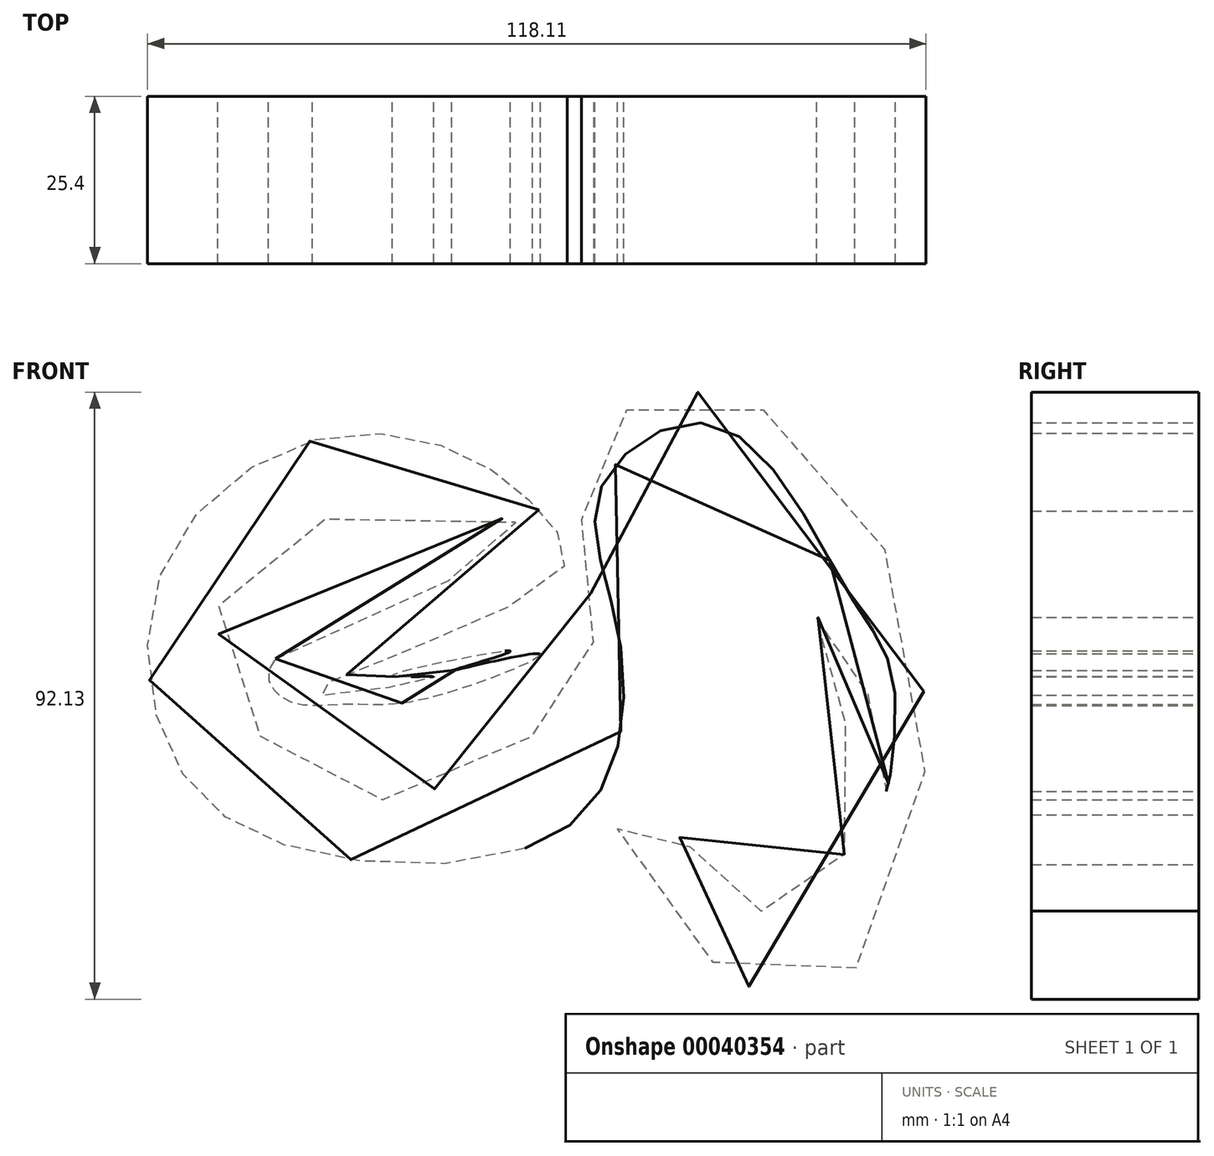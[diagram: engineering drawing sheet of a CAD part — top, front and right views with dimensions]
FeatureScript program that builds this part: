
annotation { "Feature Type Name" : "Feature", "Feature Type Description" : "" }
export const myFeature = defineFeature(function(context is Context, id is Id, definition is map)
    precondition{}
    {
        {
            var Q0;
            Q0=qCreatedBy(makeId("Front.planeOp"),FACE);
            var sketch = newSketch(context, id + "F0", { "sketchPlane" : qUnion([Q0])});
            skFitSpline(sketch, "E0", {"points": [v(-54.52, 12.7) * mm, v(-15.55, 31.2) * mm, v(-54.72, 31.6) * mm, v(-62, 11.32) * mm, v(-42.12, -8.56) * mm, v(-10.23, 6) * mm, v(-6.5, 20.96) * mm, v(-6.1, 45.57) * mm, v(16.34, 51.86) * mm, v(44.09, 4.43) * mm, v(22.83, -38.87) * mm, v(-2.56, -12.1) * mm, v(6.89, -14.47) * mm, v(17.71, -25.3) * mm, v(30.7, -19) * mm, v(31.3, 5.6) * mm, v(27.75, 19) * mm, v(36.22, 4.82) * mm, v(38.18, -7.38) * mm, v(39.37, 8.37) * mm, v(32.28, 22.93) * mm, v(12.4, 48.12) * mm, v(-5.12, 38.68) * mm, v(-2.56, 17.03) * mm, v(-8.86, -11.71) * mm, v(-48.42, -16.83) * mm, v(-69.87, -2.66) * mm, v(-71.25, 27.26) * mm, v(-46.84, 46.35) * mm, v(-23.42, 42.42) * mm, v(-12.6, 32.97) * mm, v(-12, 25.1) * mm, v(-48.81, 7.38) * mm, v(-30.5, 9.94) * mm, v(-36.8, 10.14) * mm, v(-18.9, 13.88) * mm, v(-27.75, 10.92) * mm, v(-14.57, 13.48) * mm, v(-31.89, 6.6) * mm, v(-43.9, 5.8) * mm, v(-52.75, 6.4) * mm, v(-54.52, 12.7) * mm]});
            skSolve(sketch);
        }
        {
            var Q0;
            Q0=makeQuery(id+"F0.imprint","IMPRINT",FACE,{"disambiguationData":[TD([[makeQuery(id+"F0.imprint","IMPRINT",EDGE,{"derivedFrom":sQuery(id+"F0.wireOp",EDGE,"E0")}),-1.0]])]});
            extrude(context, id + "F1", {"entities" : qUnion([Q0]), "depth" : 25.4 * mm});
        }
    });
